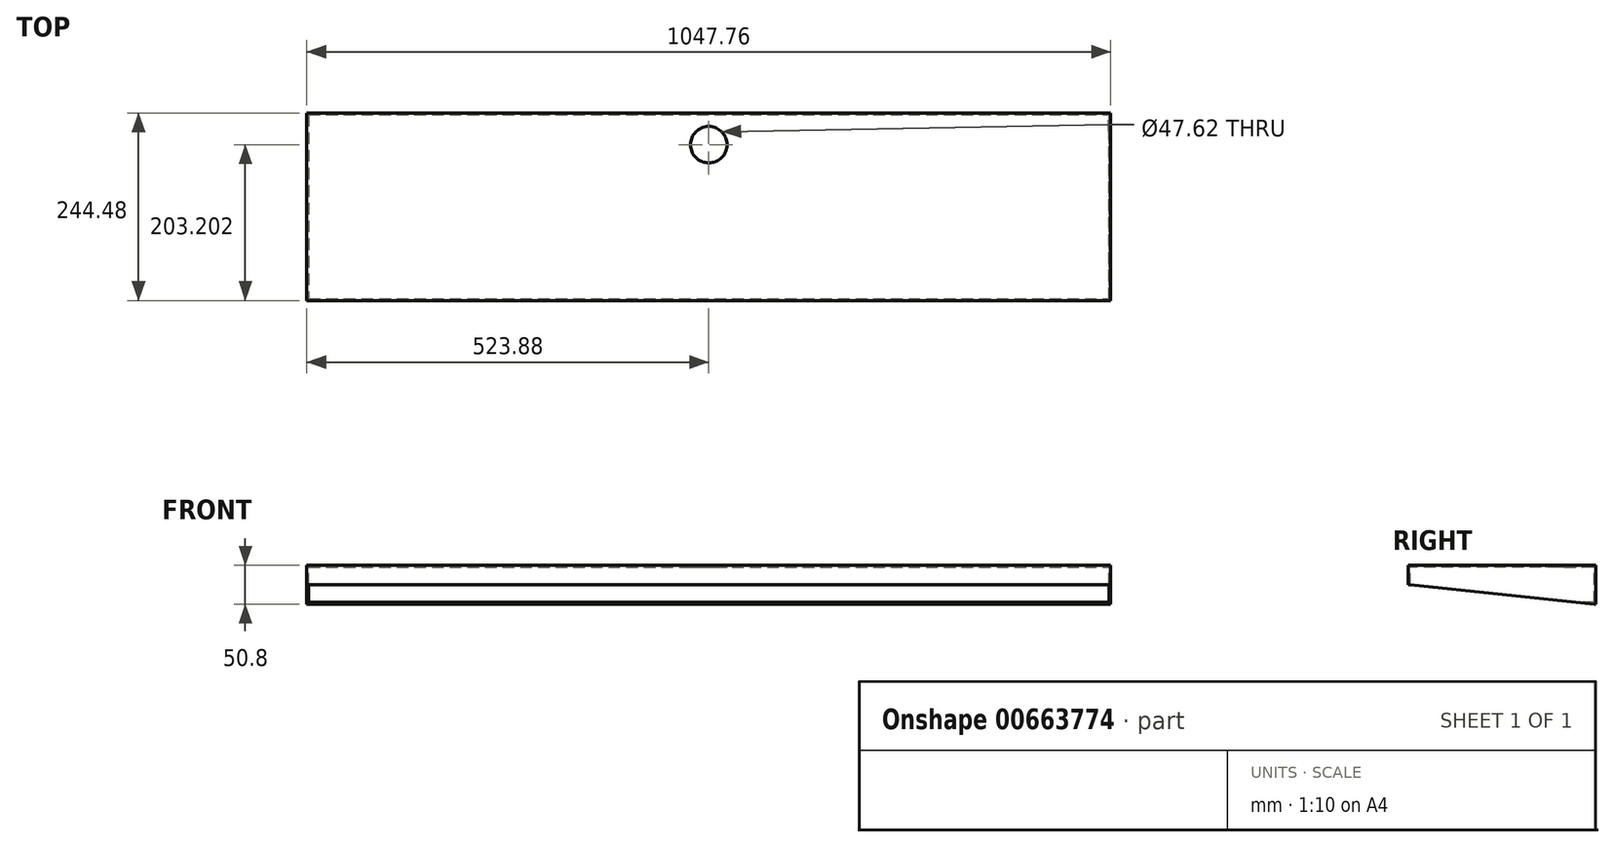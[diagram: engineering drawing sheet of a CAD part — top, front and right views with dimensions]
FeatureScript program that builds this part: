
annotation { "Feature Type Name" : "Feature", "Feature Type Description" : "" }
export const myFeature = defineFeature(function(context is Context, id is Id, definition is map)
    precondition{}
    {
        {
            var Q0;
            Q0=qCreatedBy(makeId("Top.planeOp"),FACE);
            var sketch = newSketch(context, id + "F0", { "sketchPlane" : qUnion([Q0])});
            skLineSegment(sketch, "E0.bottom", {"start": v(-523.88, 122.24) * mm, "end": v(523.88, 122.24) * mm});
            skLineSegment(sketch, "E0.top", {"start": v(-523.88, -122.24) * mm, "end": v(523.88, -122.24) * mm});
            skLineSegment(sketch, "E0.left", {"start": v(-523.88, 122.24) * mm, "end": v(-523.88, -122.24) * mm});
            skLineSegment(sketch, "E0.right", {"start": v(523.88, 122.24) * mm, "end": v(523.88, -122.24) * mm});
            skPoint(sketch, "E0.middle", {"position": v(0, 0) * mm});
            skLineSegment(sketch, "E1", {"start": v(0, 251.65) * mm, "end": v(0, -180.72) * mm, "construction": true});
            skPoint(sketch, "E1.endSnap0", {"position": v(0, -122.24) * mm});
            skLineSegment(sketch, "E2.0", {"start": v(-523.88, 80.96) * mm, "end": v(523.88, 80.96) * mm, "construction": true});
            skCircle(sketch, "E3", {"center": v(0, 80.96) * mm, "radius": 23.81 * mm});
            skSolve(sketch);
        }
        {
            var Q0;
            Q0 = qSketchRegion(id + "F0", true);
            extrude(context, id + "F1", {"entities" : qUnion([Q0]), "oppositeDirection" : true, "depth" : 50.8 * mm, "offsetDistance" : 25.4 * mm});
        }
        {
            var Q0;
            Q0=makeQuery(id+"F1.opExtrude","SWEPT_FACE",FACE,{"disambiguationData":[OSD([sQuery(id+"F0.wireOp",EDGE,"E0.right")])]});
            var sketch = newSketch(context, id + "F2", { "sketchPlane" : qUnion([Q0])});
            skLineSegment(sketch, "E4", {"start": v(-122.24, -25.4) * mm, "end": v(-119.95, -25.4) * mm});
            skLineSegment(sketch, "E5", {"start": v(-119.95, -25.4) * mm, "end": v(119.95, -50.8) * mm});
            skLineSegment(sketch, "E6", {"start": v(119.95, -50.8) * mm, "end": v(122.24, -50.8) * mm});
            skLineSegment(sketch, "E7", {"start": v(122.24, -50.8) * mm, "end": v(122.24, -106.85) * mm});
            skLineSegment(sketch, "E8", {"start": v(122.24, -106.85) * mm, "end": v(-122.24, -106.85) * mm});
            skLineSegment(sketch, "E9", {"start": v(-122.24, -106.85) * mm, "end": v(-122.24, -25.4) * mm});
            skSolve(sketch);
        }
        {
            var Q0;
            Q0 = qSketchRegion(id + "F2", true);
            extrude(context, id + "F3", {"entities" : qUnion([Q0]), "operationType" : NewBodyOperationType.REMOVE, "endBound" : BoundingType.THROUGH_ALL, "oppositeDirection" : true, "depth" : 25.4 * mm, "offsetDistance" : 25.4 * mm});
        }
        {
            var Q0;
            Q0=makeQuery(id+"F3.boolean.opBoolean","COPY",FACE,{"derivedFrom":makeQuery(id+"F3.opExtrude","SWEPT_FACE",FACE,{"disambiguationData":[OSD([sQuery(id+"F2.wireOp",EDGE,"E5")])]})});
            shell(context, id + "F4", {"entities" : qUnion([Q0]), "thickness" : 2.3 * mm});
        }
        {
            var Q0;
            {var subQ0=sQuery(id+"F0.wireOp",EDGE,"E3");var subQ1=sQuery(id+"F0.wireOp",EDGE,"E0.right");var subQ2=sQuery(id+"F0.wireOp",EDGE,"E0.left");var subQ3=sQuery(id+"F0.wireOp",EDGE,"E0.top");var subQ4=sQuery(id+"F0.wireOp",EDGE,"E0.bottom");Q0=makeQuery(id+"F4.opShell","OFFSET_FACE",FACE,{"disambiguationData":[OSD([subQ4,subQ3,subQ2,subQ1,subQ0]),TDD([makeQuery(id+"F1.opExtrude","CAP_FACE",FACE,{"disambiguationData":[OSD([subQ4,subQ3,subQ2,subQ1,subQ0])],"isStart":true})])]});}
            var sketch = newSketch(context, id + "F5", { "sketchPlane" : qUnion([Q0])});
            skCircle(sketch, "E10", {"center": v(0, -80.96) * mm, "radius": 33.49 * mm});
            skSolve(sketch);
        }
        {
            var Q0;
            Q0 = qSketchRegion(id + "F5", true);
            extrude(context, id + "F6", {"entities" : qUnion([Q0]), "operationType" : NewBodyOperationType.REMOVE, "endBound" : BoundingType.THROUGH_ALL, "depth" : 25.4 * mm, "offsetDistance" : 25.4 * mm});
        }
        {
            var Q0;
            Q0=makeQuery(id+"F3.boolean.opBoolean","COPY",FACE,{"derivedFrom":makeQuery(id+"F3.opExtrude","SWEPT_FACE",FACE,{"disambiguationData":[OSD([sQuery(id+"F2.wireOp",EDGE,"E5")])]})});
            var sketch = newSketch(context, id + "F7", { "sketchPlane" : qUnion([Q0])});
            skLineSegment(sketch, "E11.0", {"start": v(-521.59, -102.92) * mm, "end": v(-521.59, 116.61) * mm, "construction": true});
            skLineSegment(sketch, "E12.0", {"start": v(-523.88, -124.63) * mm, "end": v(523.88, -124.63) * mm, "construction": true});
            skLineSegment(sketch, "E13.bottom", {"start": v(-521.59, -102.92) * mm, "end": v(521.2, -102.92) * mm});
            skLineSegment(sketch, "E13.top", {"start": v(-521.59, -124.63) * mm, "end": v(521.2, -124.63) * mm});
            skLineSegment(sketch, "E13.left", {"start": v(-521.59, -102.92) * mm, "end": v(-521.59, -124.63) * mm});
            skLineSegment(sketch, "E13.right", {"start": v(521.2, -102.92) * mm, "end": v(521.2, -124.63) * mm});
            skSolve(sketch);
        }
        {
            var Q0;
            Q0 = qSketchRegion(id + "F7", true);
            extrude(context, id + "F8", {"entities" : qUnion([Q0]), "operationType" : NewBodyOperationType.REMOVE, "oppositeDirection" : true, "depth" : 2.41 * mm, "offsetDistance" : 25.4 * mm});
        }
    });
